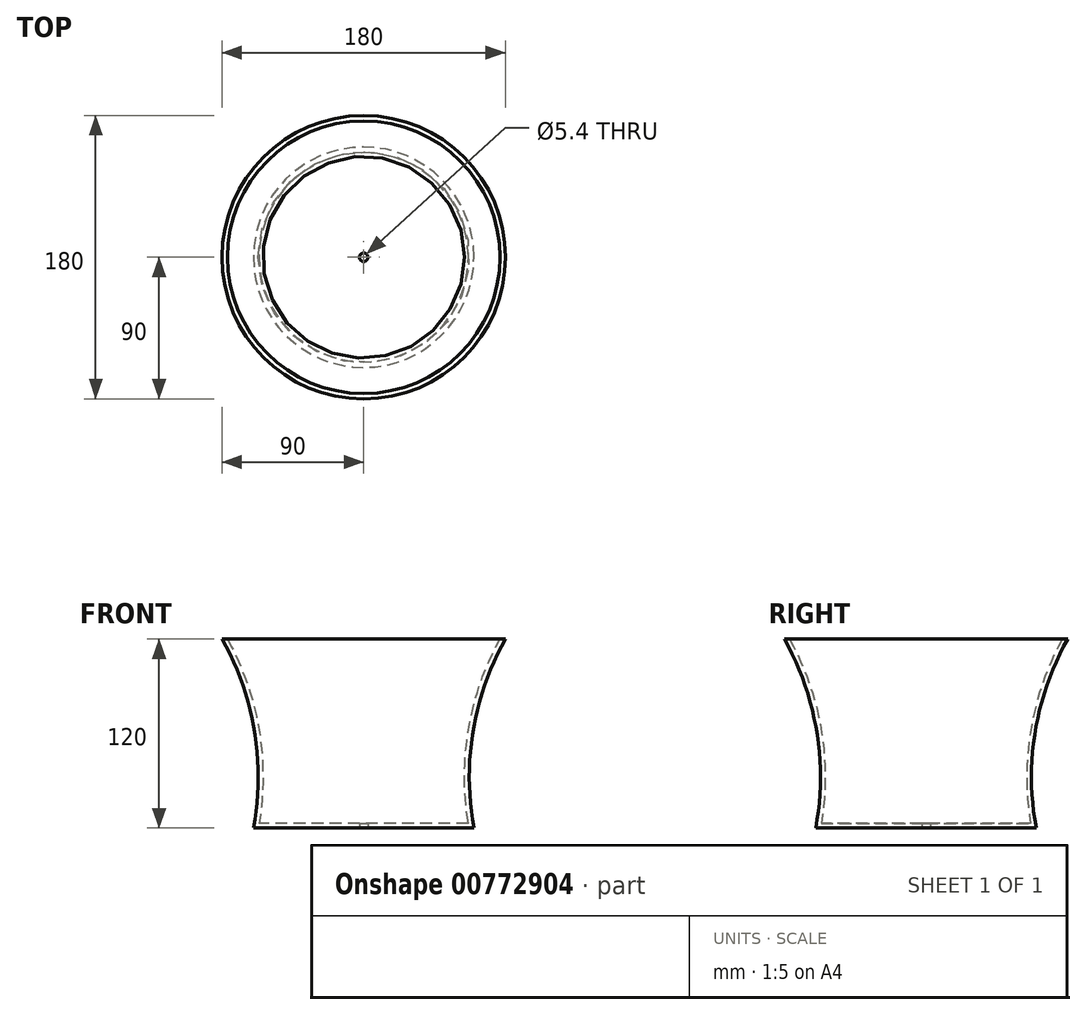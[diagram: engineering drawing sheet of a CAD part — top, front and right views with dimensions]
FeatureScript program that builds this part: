
annotation { "Feature Type Name" : "Feature", "Feature Type Description" : "" }
export const myFeature = defineFeature(function(context is Context, id is Id, definition is map)
    precondition{}
    {
        {
            var Q0;
            Q0=qCreatedBy(makeId("Front.planeOp"),FACE);
            var sketch = newSketch(context, id + "F0", { "sketchPlane" : qUnion([Q0])});
            skLineSegment(sketch, "E0", {"start": v(0, 0) * mm, "end": v(0, 120) * mm});
            skLineSegment(sketch, "E1", {"start": v(0, 120) * mm, "end": v(90, 120) * mm});
            skLineSegment(sketch, "E2", {"start": v(90, 120) * mm, "end": v(-90, 120) * mm});
            skLineSegment(sketch, "E3", {"start": v(0, 0) * mm, "end": v(70, 0) * mm});
            skLineSegment(sketch, "E4", {"start": v(70, 0) * mm, "end": v(-70, 0) * mm});
            skArc(sketch, "E5", {"start": v(-70, 0) * mm, "mid": v(-69.46, 61.76) * mm, "end": v(-90, 120) * mm});
            skSolve(sketch);
        }
        {
            var Q0;
            Q0=makeQuery(id+"F0.imprint","IMPRINT",FACE,{"disambiguationData":[TD([[makeQuery(id+"F0.imprint","IMPRINT",EDGE,{"derivedFrom":sQuery(id+"F0.wireOp",EDGE,"E0")}),1.0]])]});
            var Q1;
            Q1=sQuery(id+"F0.wireOp",EDGE,"E0");
            revolve(context, id + "F1", {"surfaceOperationType" : NewSurfaceOperationType.NEW, "entities" : qUnion([Q0]), "axis" : qUnion([Q1]), "revolveType" : RevolveType.FULL});
        }
        {
            var Q0;
            Q0=makeQuery(id+"F1.opRevolve","SWEPT_FACE",FACE,{"disambiguationData":[OSD([sQuery(id+"F0.wireOp",EDGE,"E2")])]});
            shell(context, id + "F2", {"entities" : qUnion([Q0]), "thickness" : 3 * mm});
        }
        {
            var Q0;
            Q0=makeQuery(id+"F1.opRevolve","SWEPT_FACE",FACE,{"disambiguationData":[OSD([sQuery(id+"F0.wireOp",EDGE,"E4")])]});
            var sketch = newSketch(context, id + "F3", { "sketchPlane" : qUnion([Q0])});
            skCircle(sketch, "E6", {"center": v(0, 0) * mm, "radius": 2.7 * mm});
            skSolve(sketch);
        }
        {
            var Q0;
            Q0=makeQuery(id+"F3.imprint","IMPRINT",FACE,{"disambiguationData":[TD([[makeQuery(id+"F3.imprint","IMPRINT",EDGE,{"derivedFrom":sQuery(id+"F3.wireOp",EDGE,"E6")}),1.0]])]});
            extrude(context, id + "F4", {"entities" : qUnion([Q0]), "operationType" : NewBodyOperationType.REMOVE, "oppositeDirection" : true, "depth" : 25 * mm, "offsetDistance" : 25 * mm});
        }
    });
